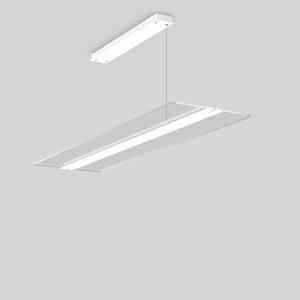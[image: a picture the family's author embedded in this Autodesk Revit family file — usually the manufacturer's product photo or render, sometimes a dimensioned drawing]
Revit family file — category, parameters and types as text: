
# Revit family: twindot_s_312263_002_730_171f
name_source: partatom
category: Lighting Fixtures
units: mm (PartAtom-declared; Revit-internal decimal feet)

## family parameters
Cut with Voids When Loaded = No
Host = Face
Light Source = No
Part Type = Normal
Room Calculation Point = No
Round Connector Dimension = Use Diameter
Shared = No

## types (1)
- TWINDOT S (1 x LED Modul 830, 6500 lm, 3000)
    Apparent Load = 57 VA
    CIE Flux Codes = 47 77 94 55 100
    Color Rendering = 80
    Color Temperature = 3000
    Default Elevation = 1800 mm
    Description = Series: TWINDOT S
LED pendant luminaire with extremely flat and frameless appearance. Middle bar made of aluminium extrusion profile, powder-coated. Transparent light guide made of UV-resistant acrylic glass (PMMA) with TWINDOT prismatic. Light control with perfectly glare-free TWINDOT technology for pleasantly gentle light with soft shadows. Even and wide indirect and direct light distribution. Direct 55%, indirect 45% light emission. 4-point steel cable suspension, steplessly adjustable. Converter integrated in the canopy (powder-coated white). Power supply through suspension cable. 
Colour: traffic white, matt (RAL 9016)
Length: 1200 mm
Width: 350 mm
Height: 20 mm
Suspension length: 500-1200 mm
Lamp: LED
Socket: without socket
Colour temperature: 3000K
Colour rendering index (CRI): 80
System power: 57 W
Rated luminous flux: 6500 lm
Luminous efficiency: 114 lm/W
Control gear: Dimmable Bluetooth converter
Protection class: I
Type of protection: IP 20
    Height = 20 mm  [stored 0.0656168 ft]
    Lamp = 1 x LED Modul 830
    Lamp Light Flux = 6500 lm
    Lamp count = 1
    Length = 1200 mm
    Lifetime = 50000 h
    Luminous efficacy = 114 lm/W
    Manufacturer = RZB
    ModVariant = No
    Model = 312263.002.730
    Mounting Place = Ceiling
    Mounting Type = Pendant
    Number of Poles = 1
    OnlyDefault = Yes
    Power Factor = 1
    Product Name = TWINDOT S
    Product group = Pendant modular luminaires
    ProductGroupID = 906
    Protection Class = Protection class I
    Protection Degree = IP 20
    RLX_Detail_Level = 1
    RLX_Emergency_Light_Flux = 0 lm
    RLX_Emergency_Type = 0
    RLX_Emergency_Type_DB = No
    RlxData = <blob elided: 35265 chars, md5=6783e45e>
    Socket = socket
    Standby Power = 0 W
    System Light Flux = 6500 lm
    System Power = 57 W
    Type Comments = Product without accessories
    Type Image = 312263.002.jpg
    URL = http://relux.com
    VarID = ---
    Voltage = 230 V
    Voltage Range = 220-240 V
    Weight = 0.00 kg
    Width = 350 mm

note: [stored X ft] marks values corroborated as IEEE doubles in the binary element streams (Revit-internal decimal feet)

## geometry (parser evidence)
native form markers: Blend x4, Sweep x12
no freeform markers — native parametric forms only
